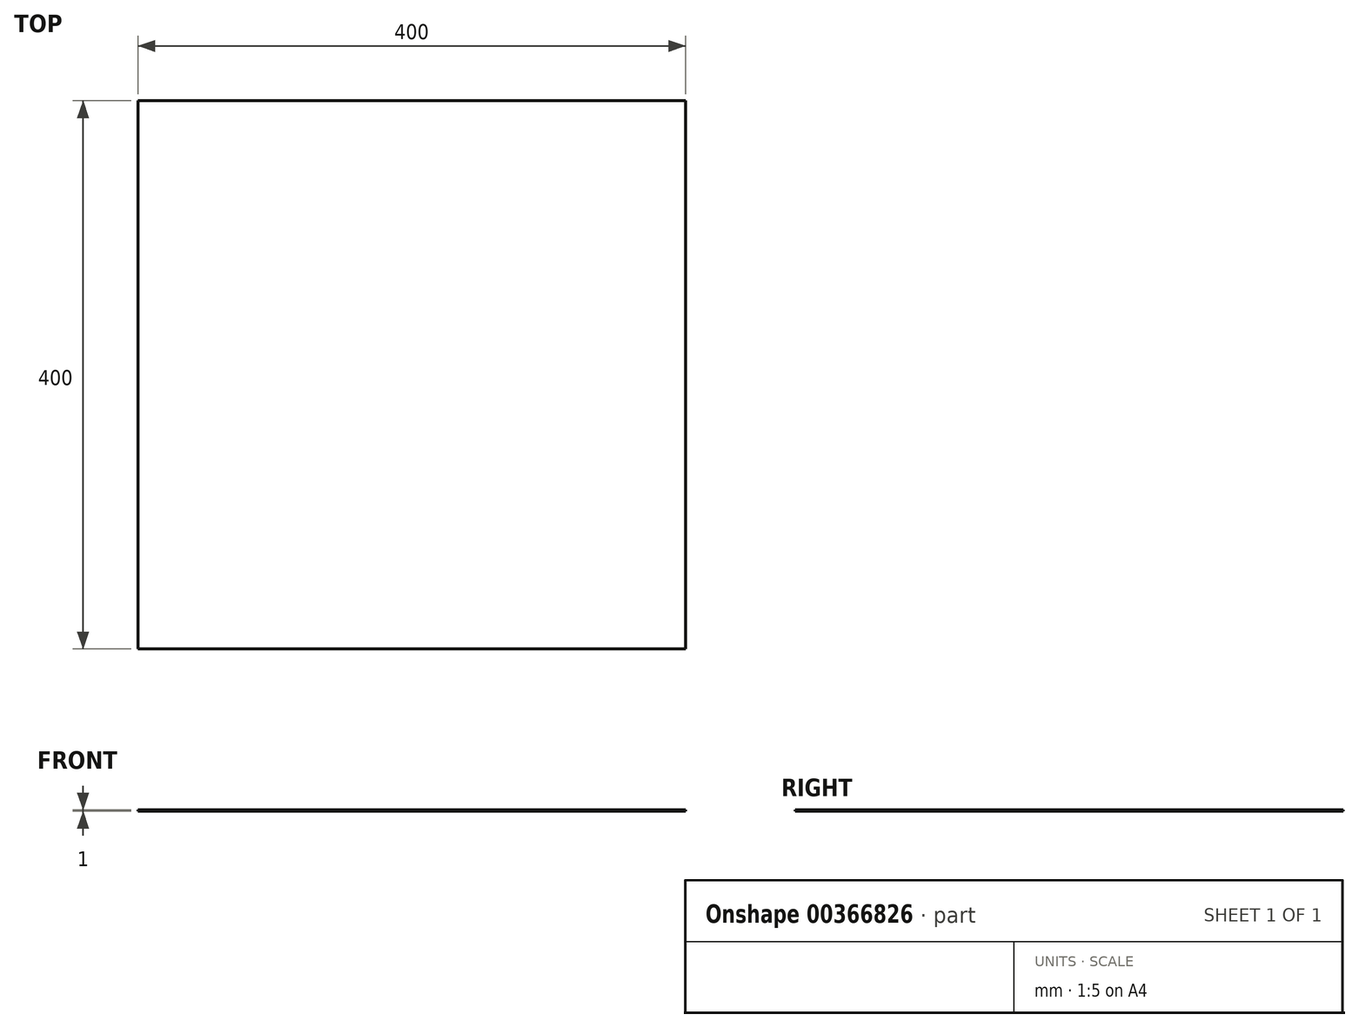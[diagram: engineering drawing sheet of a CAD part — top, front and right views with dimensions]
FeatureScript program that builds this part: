
annotation { "Feature Type Name" : "Feature", "Feature Type Description" : "" }
export const myFeature = defineFeature(function(context is Context, id is Id, definition is map)
    precondition{}
    {
        {
            var Q0;
            Q0=qCreatedBy(makeId("Top.planeOp"),FACE);
            var sketch = newSketch(context, id + "F0", { "sketchPlane" : qUnion([Q0])});
            skLineSegment(sketch, "E0.bottom", {"start": v(-338.11, 218.05) * mm, "end": v(61.89, 218.05) * mm});
            skLineSegment(sketch, "E0.top", {"start": v(-338.11, -181.95) * mm, "end": v(61.89, -181.95) * mm});
            skLineSegment(sketch, "E0.left", {"start": v(-338.11, 218.05) * mm, "end": v(-338.11, -181.95) * mm});
            skLineSegment(sketch, "E0.right", {"start": v(61.89, 218.05) * mm, "end": v(61.89, -181.95) * mm});
            skSolve(sketch);
        }
        {
            var Q0;
            Q0=makeQuery(id+"F0.imprint","IMPRINT",FACE,{"disambiguationData":[TD([[makeQuery(id+"F0.imprint","IMPRINT",EDGE,{"derivedFrom":sQuery(id+"F0.wireOp",EDGE,"E0.bottom")}),-1.0]])]});
            extrude(context, id + "F1", {"entities" : qUnion([Q0]), "depth" : 1 * mm});
        }
    });
